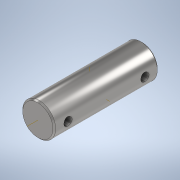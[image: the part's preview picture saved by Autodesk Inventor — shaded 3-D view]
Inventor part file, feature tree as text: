
AUTODESK INVENTOR PART (.ipt)
format: ipt  version: 2021.1 (Build 251245000, 245)  size: 135,168 bytes
history: native  units: in
note: dims shown in document units (in); Inventor stores cm internally (conversion verified against a paired STEP export)
features: extrude x2, sketch x2, projected_geometry x2, chamfer x1
ambient origin geometry x8: Origin, YZ Plane, XZ Plane, XY Plane, X Axis, Y Axis, Z Axis, Center Point
bodies: Solid1 (feature_tree)
feature tree (7):
  extrude  "Extrusion1"  Depth=3.8in TaperAngle=0.0deg
  extrude  "Extrusion2"  Depth=0.3in
  chamfer  "Chamfer1"  Distance=0.5in
  sketch  "Sketch1"  dims[d0=1.2in d1=3.8in d2=0.0in]
  sketch  "Sketch2"  dims[d3=0.3in d4=0.3in d5=0.5in d6=0.5in d7=0.0in d8=0.0in d9=0.05in d10=0.125in d11=45.0deg]
  projected_geometry  "Projected Loop1"
  projected_geometry  "Project Cut Edges1"
